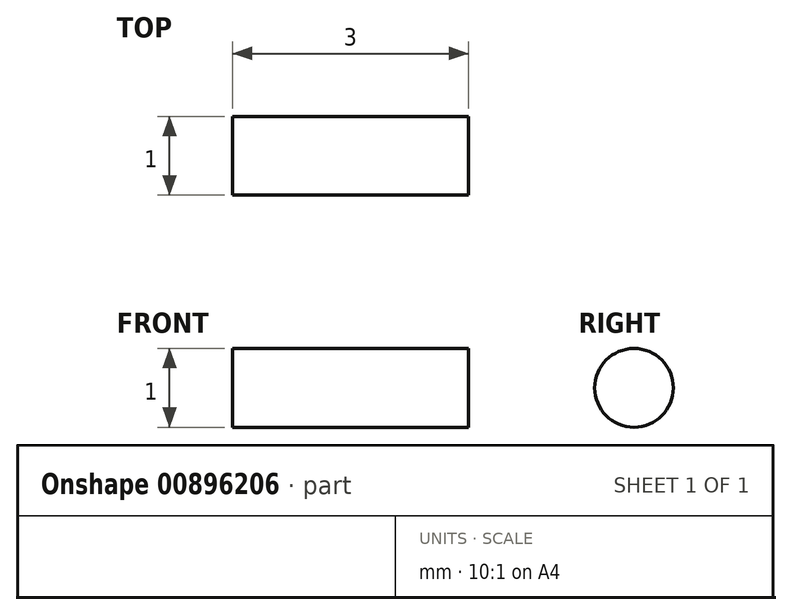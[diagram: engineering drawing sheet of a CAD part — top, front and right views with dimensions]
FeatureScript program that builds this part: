
annotation { "Feature Type Name" : "Feature", "Feature Type Description" : "" }
export const myFeature = defineFeature(function(context is Context, id is Id, definition is map)
    precondition{}
    {
        {
            var Q0;
            Q0=qCreatedBy(makeId("Right.planeOp"),FACE);
            var sketch = newSketch(context, id + "F0", { "sketchPlane" : qUnion([Q0])});
            skCircle(sketch, "E0", {"center": v(0, 0) * mm, "radius": 0.5 * mm});
            skSolve(sketch);
        }
        {
            var Q0;
            Q0 = qSketchRegion(id + "F0", true);
            extrude(context, id + "F1", {"entities" : qUnion([Q0]), "depth" : 3 * mm, "offsetDistance" : 25 * mm});
        }
    });
